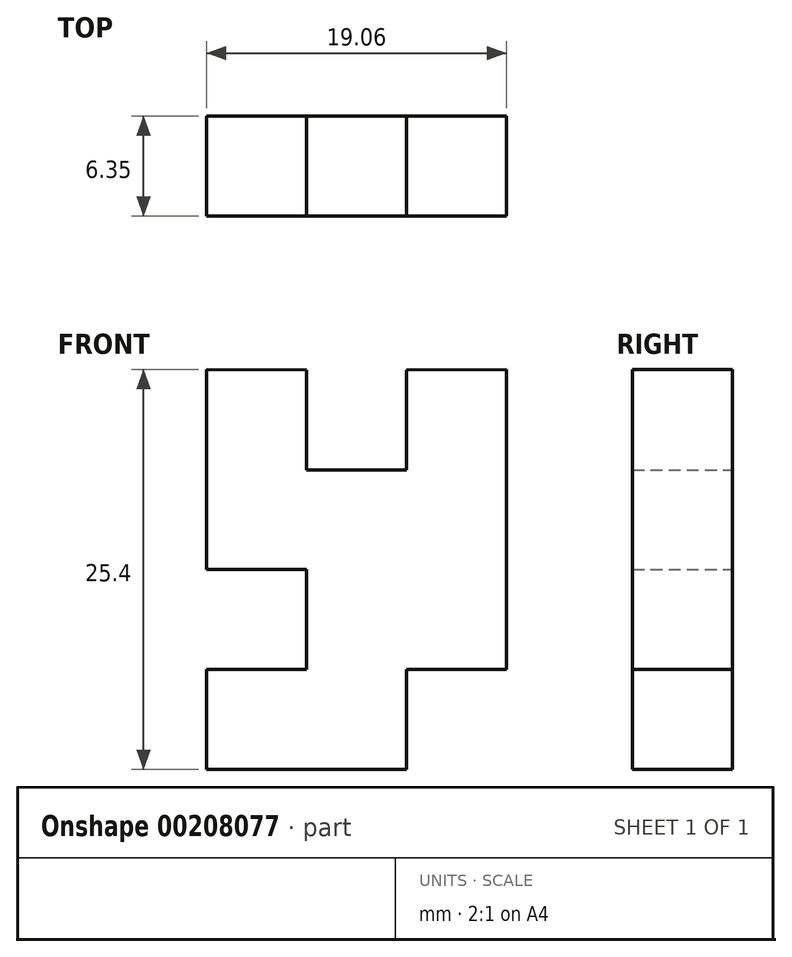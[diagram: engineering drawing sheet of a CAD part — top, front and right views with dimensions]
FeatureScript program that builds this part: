
annotation { "Feature Type Name" : "Feature", "Feature Type Description" : "" }
export const myFeature = defineFeature(function(context is Context, id is Id, definition is map)
    precondition{}
    {
        {
            var Q0;
            Q0=qCreatedBy(makeId("Front.planeOp"),FACE);
            var sketch = newSketch(context, id + "F0", { "sketchPlane" : qUnion([Q0])});
            skLineSegment(sketch, "E0.top", {"start": v(3.18, -12.7) * mm, "end": v(-9.53, -12.7) * mm});
            skLineSegment(sketch, "E0.left", {"start": v(9.53, 12.7) * mm, "end": v(9.53, -6.35) * mm});
            skLineSegment(sketch, "E0.right", {"start": v(-9.52, 12.7) * mm, "end": v(-9.52, 0) * mm});
            skPoint(sketch, "E0.middle", {"position": v(0, 0) * mm});
            skLineSegment(sketch, "E1.top", {"start": v(9.52, -6.35) * mm, "end": v(3.17, -6.35) * mm});
            skLineSegment(sketch, "E1.right", {"start": v(3.18, -12.7) * mm, "end": v(3.17, -6.35) * mm});
            skLineSegment(sketch, "E2.bottom", {"start": v(3.17, 6.3) * mm, "end": v(-3.18, 6.3) * mm});
            skLineSegment(sketch, "E2.left", {"start": v(3.17, 6.3) * mm, "end": v(3.17, 12.66) * mm});
            skLineSegment(sketch, "E2.right", {"start": v(-3.18, 6.3) * mm, "end": v(-3.18, 12.66) * mm});
            skLineSegment(sketch, "E3.bottom", {"start": v(-3.19, -6.35) * mm, "end": v(-9.54, -6.35) * mm});
            skLineSegment(sketch, "E3.top", {"start": v(-3.19, 0) * mm, "end": v(-9.54, 0) * mm});
            skLineSegment(sketch, "E3.left", {"start": v(-3.19, -6.35) * mm, "end": v(-3.19, 0) * mm});
            skLineSegment(sketch, "E4.trimOffspring", {"start": v(-9.53, -6.35) * mm, "end": v(-9.53, -12.7) * mm});
            skLineSegment(sketch, "E5", {"start": v(-9.52, 12.7) * mm, "end": v(-3.18, 12.66) * mm});
            skLineSegment(sketch, "E6", {"start": v(3.17, 12.66) * mm, "end": v(9.53, 12.7) * mm});
            skPoint(sketch, "E7.orphan", {"position": v(9.52, -12.7) * mm});
            skSolve(sketch);
        }
        {
            var Q0;
            Q0=makeQuery(id+"F0.imprint","IMPRINT",FACE,{"disambiguationData":[TD([[makeQuery(id+"F0.imprint","IMPRINT",EDGE,{"derivedFrom":sQuery(id+"F0.wireOp",EDGE,"E0.top")}),-1.0]])]});
            extrude(context, id + "F1", {"entities" : qUnion([Q0]), "depth" : 6.35 * mm});
        }
    });
